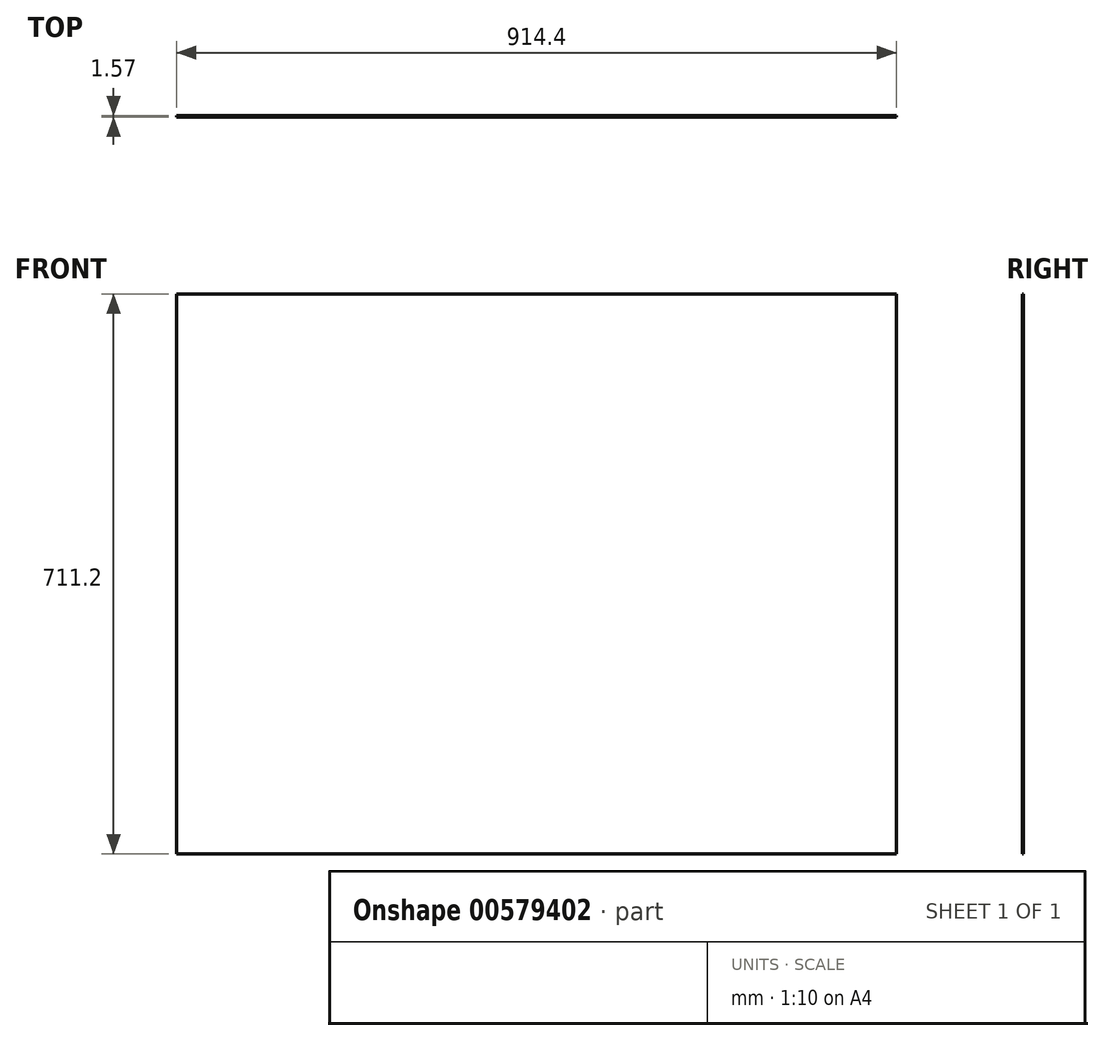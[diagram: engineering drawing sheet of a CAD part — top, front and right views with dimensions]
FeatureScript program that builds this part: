
annotation { "Feature Type Name" : "Feature", "Feature Type Description" : "" }
export const myFeature = defineFeature(function(context is Context, id is Id, definition is map)
    precondition{}
    {
        {
            var Q0;
            Q0=qCreatedBy(makeId("Front.planeOp"),FACE);
            var sketch = newSketch(context, id + "F0", { "sketchPlane" : qUnion([Q0])});
            skLineSegment(sketch, "E0.bottom", {"start": v(-454.3, 465.8) * mm, "end": v(460.1, 465.8) * mm});
            skLineSegment(sketch, "E0.top", {"start": v(-454.3, -245.4) * mm, "end": v(460.1, -245.4) * mm});
            skLineSegment(sketch, "E0.left", {"start": v(-454.3, 465.8) * mm, "end": v(-454.3, -245.4) * mm});
            skLineSegment(sketch, "E0.right", {"start": v(460.1, 465.8) * mm, "end": v(460.1, -245.4) * mm});
            skSolve(sketch);
        }
        {
            var Q0;
            Q0 = qSketchRegion(id + "F0", true);
            extrude(context, id + "F1", {"entities" : qUnion([Q0]), "depth" : 1.57 * mm, "offsetDistance" : 25.4 * mm});
        }
    });
